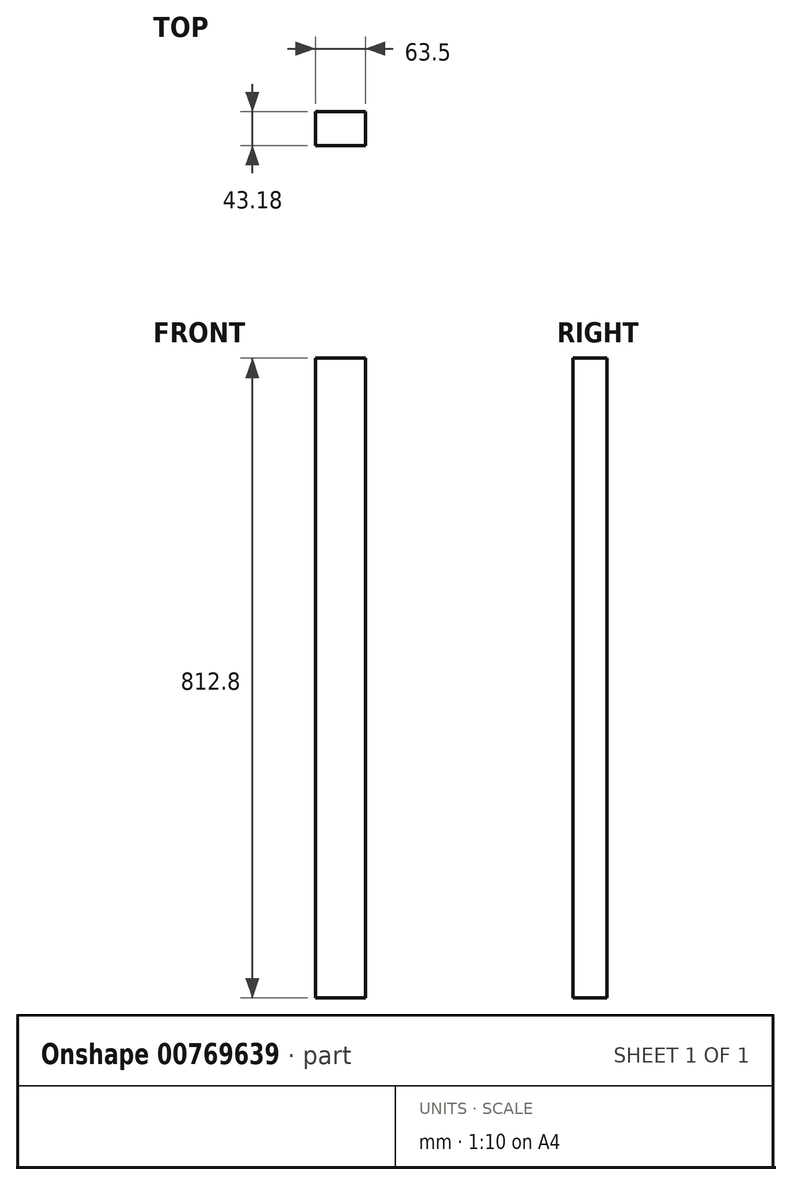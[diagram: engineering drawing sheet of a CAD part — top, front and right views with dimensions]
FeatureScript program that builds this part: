
annotation { "Feature Type Name" : "Feature", "Feature Type Description" : "" }
export const myFeature = defineFeature(function(context is Context, id is Id, definition is map)
    precondition{}
    {
        {
            var Q0;
            Q0=qCreatedBy(makeId("Top.planeOp"),FACE);
            var sketch = newSketch(context, id + "F0", { "sketchPlane" : qUnion([Q0])});
            skLineSegment(sketch, "E0.bottom", {"start": v(-31.75, 21.59) * mm, "end": v(31.75, 21.59) * mm});
            skLineSegment(sketch, "E0.top", {"start": v(-31.75, -21.6) * mm, "end": v(31.75, -21.6) * mm});
            skLineSegment(sketch, "E0.left", {"start": v(-31.75, 21.59) * mm, "end": v(-31.75, -21.6) * mm});
            skLineSegment(sketch, "E0.right", {"start": v(31.75, 21.59) * mm, "end": v(31.75, -21.6) * mm});
            skPoint(sketch, "E0.middle", {"position": v(0, 0) * mm});
            skSolve(sketch);
        }
        {
            var Q0;
            Q0 = qSketchRegion(id + "F0", true);
            extrude(context, id + "F1", {"entities" : qUnion([Q0]), "depth" : 812.8 * mm, "offsetDistance" : 25.4 * mm});
        }
    });
